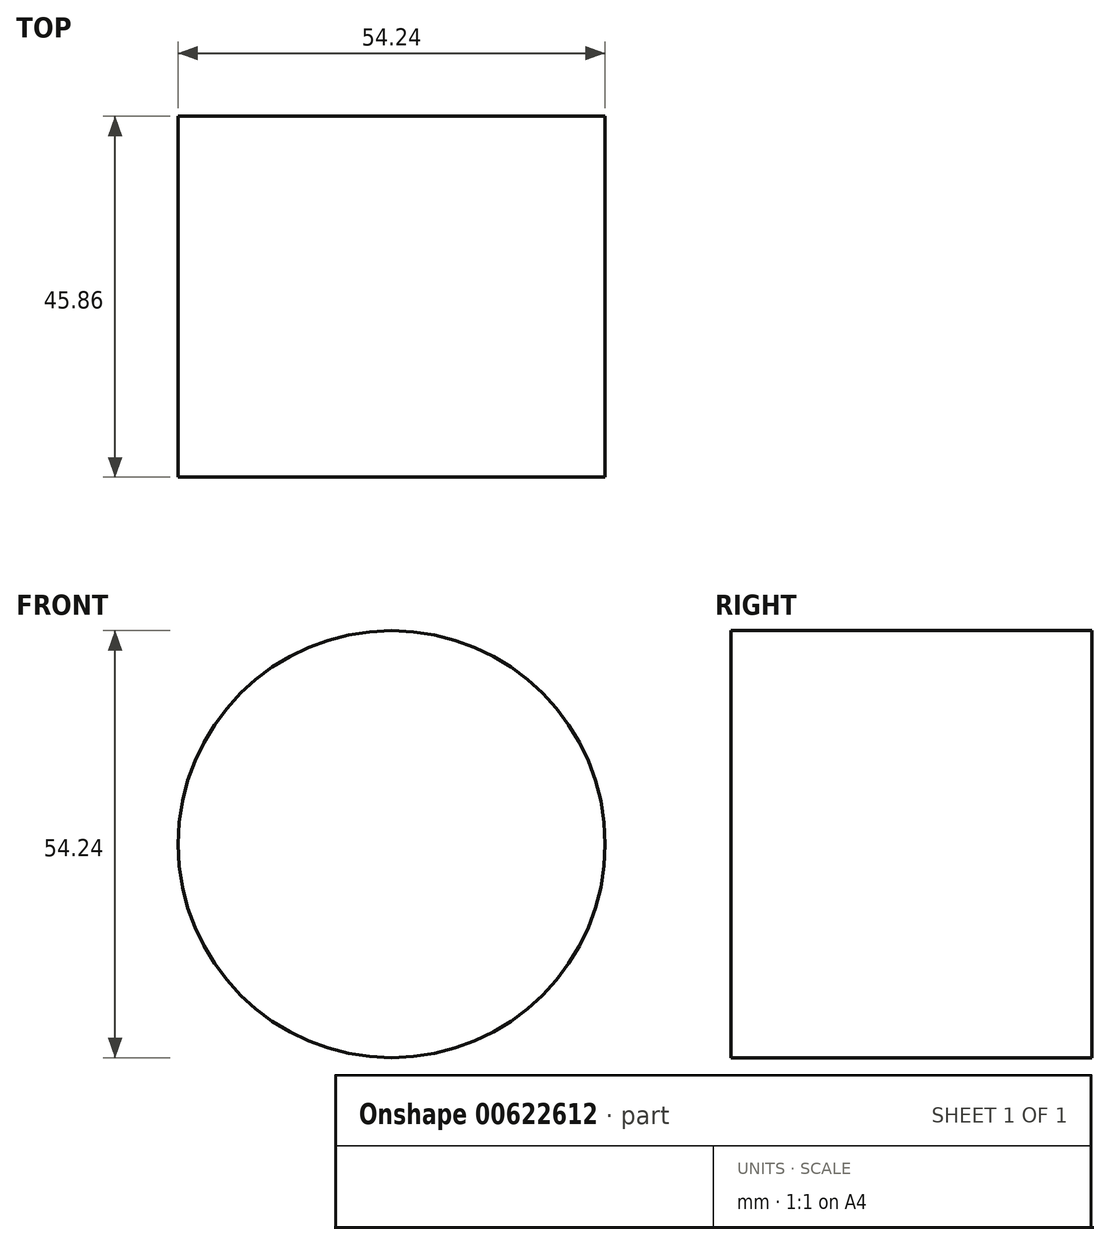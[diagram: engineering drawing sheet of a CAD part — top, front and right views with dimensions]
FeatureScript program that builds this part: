
annotation { "Feature Type Name" : "Feature", "Feature Type Description" : "" }
export const myFeature = defineFeature(function(context is Context, id is Id, definition is map)
    precondition{}
    {
        {
            var Q0;
            Q0=qCreatedBy(makeId("Front.planeOp"),FACE);
            var sketch = newSketch(context, id + "F0", { "sketchPlane" : qUnion([Q0])});
            skCircle(sketch, "E0", {"center": v(0, 0) * mm, "radius": 27.12 * mm});
            skSolve(sketch);
        }
        {
            var Q0;
            Q0=makeQuery(id+"F0.imprint","IMPRINT",FACE,{"disambiguationData":[TD([[makeQuery(id+"F0.imprint","IMPRINT",EDGE,{"derivedFrom":sQuery(id+"F0.wireOp",EDGE,"E0")}),1.0]])]});
            extrude(context, id + "F1", {"entities" : qUnion([Q0]), "depth" : 45.86 * mm, "offsetDistance" : 25.4 * mm});
        }
    });
